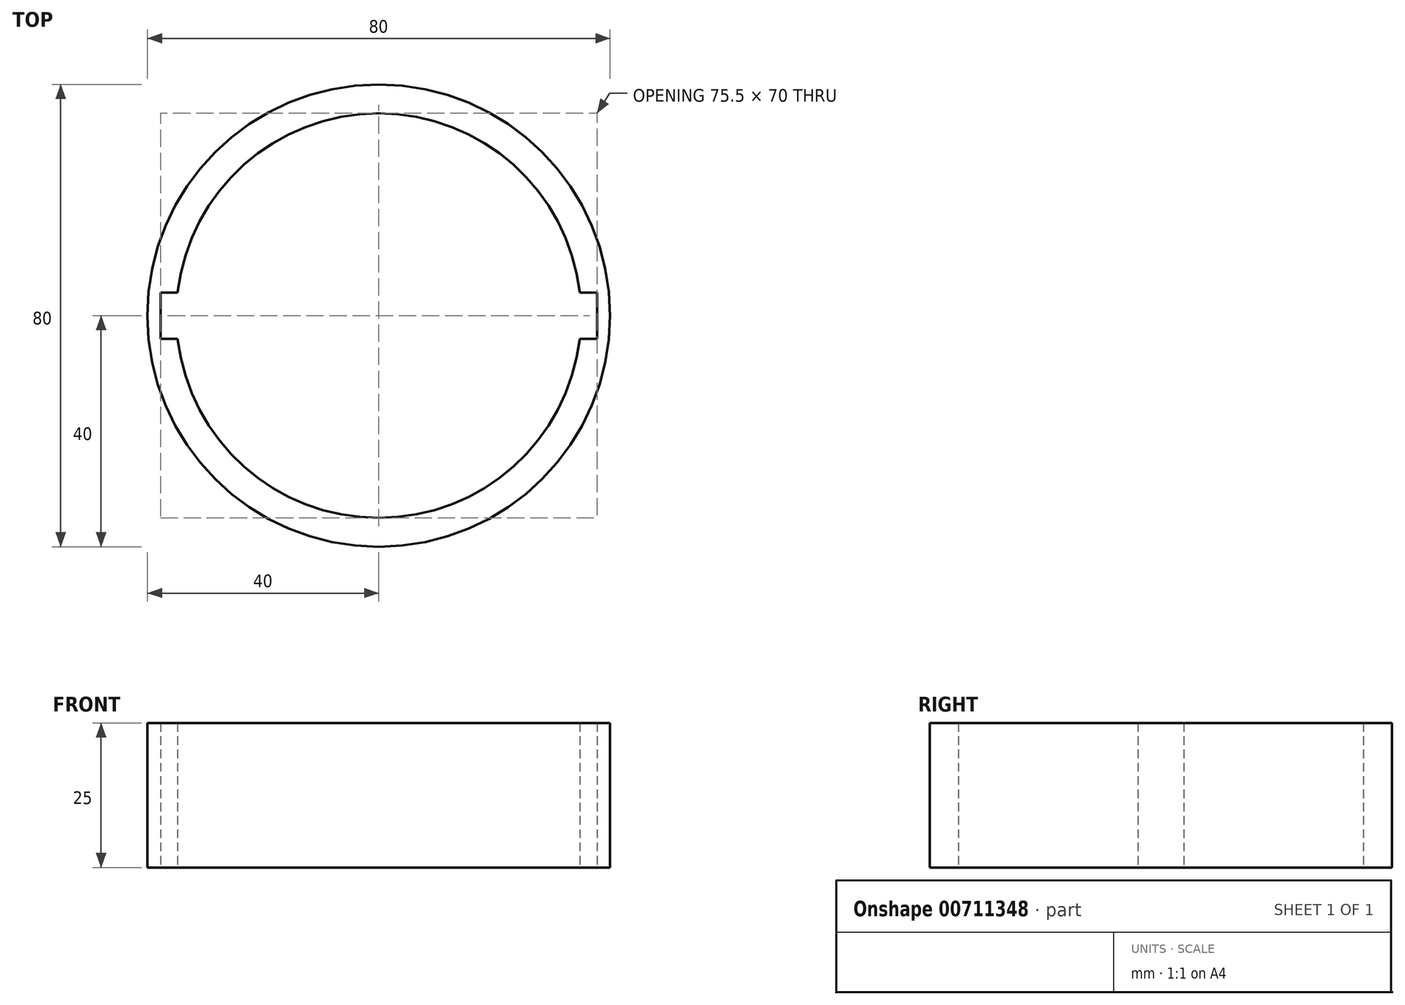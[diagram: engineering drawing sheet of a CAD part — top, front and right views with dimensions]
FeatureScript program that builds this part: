
annotation { "Feature Type Name" : "Feature", "Feature Type Description" : "" }
export const myFeature = defineFeature(function(context is Context, id is Id, definition is map)
    precondition{}
    {
        {
            var Q0;
            Q0=qCreatedBy(makeId("Top.planeOp"),FACE);
            var sketch = newSketch(context, id + "F0", { "sketchPlane" : qUnion([Q0])});
            skCircle(sketch, "E0", {"center": v(0, 0) * mm, "radius": 40 * mm});
            skLineSegment(sketch, "E1.bottom", {"start": v(37.75, -4) * mm, "end": v(-37.75, -4) * mm});
            skLineSegment(sketch, "E1.top", {"start": v(37.75, 4) * mm, "end": v(-37.75, 4) * mm});
            skLineSegment(sketch, "E1.left", {"start": v(37.75, -4) * mm, "end": v(37.75, 4) * mm});
            skLineSegment(sketch, "E1.right", {"start": v(-37.75, -4) * mm, "end": v(-37.75, 4) * mm});
            skCircle(sketch, "E2", {"center": v(0, 0) * mm, "radius": 35 * mm});
            skLineSegment(sketch, "E3.bottom", {"start": v(6.5, 3) * mm, "end": v(-6.5, 3) * mm});
            skLineSegment(sketch, "E3.top", {"start": v(6.5, -3) * mm, "end": v(-6.5, -3) * mm});
            skLineSegment(sketch, "E3.left", {"start": v(6.5, 3) * mm, "end": v(6.5, -3) * mm});
            skLineSegment(sketch, "E3.right", {"start": v(-6.5, 3) * mm, "end": v(-6.5, -3) * mm});
            skSolve(sketch);
        }
        {
            var Q0;
            Q0=makeQuery(id+"F0.imprint","IMPRINT",FACE,{"disambiguationData":[TD([[makeQuery(id+"F0.imprint","IMPRINT",EDGE,{"derivedFrom":sQuery(id+"F0.wireOp",EDGE,"E0")}),1.0]])]});
            extrude(context, id + "F1", {"entities" : qUnion([Q0]), "depth" : 25 * mm, "offsetDistance" : 25 * mm});
        }
    });
